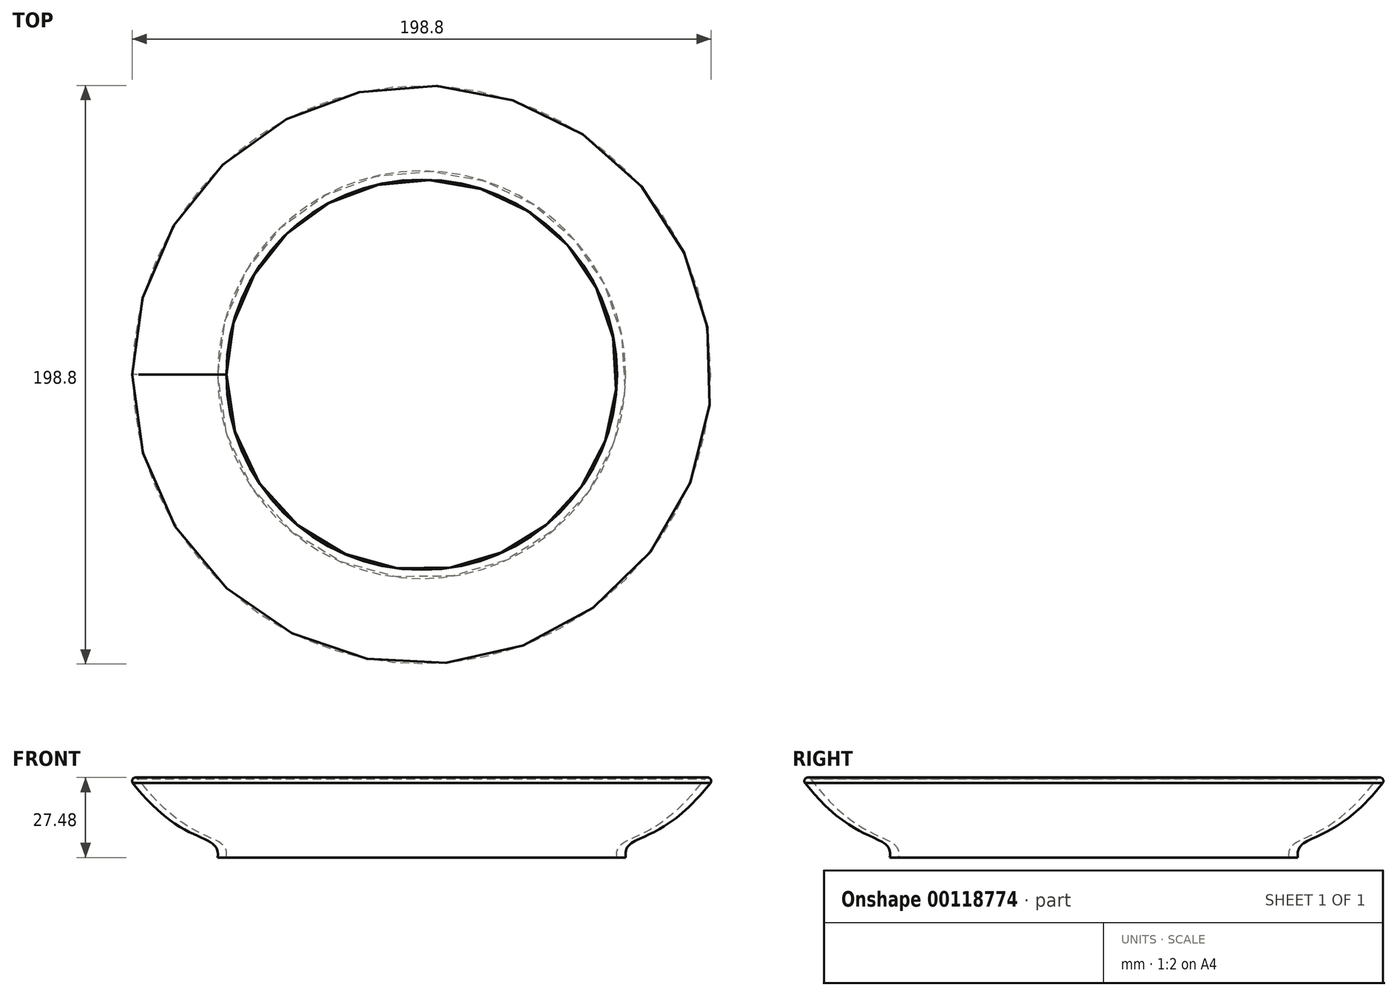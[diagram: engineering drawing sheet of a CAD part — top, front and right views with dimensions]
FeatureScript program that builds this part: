
annotation { "Feature Type Name" : "Feature", "Feature Type Description" : "" }
export const myFeature = defineFeature(function(context is Context, id is Id, definition is map)
    precondition{}
    {
        {
            var Q0;
            Q0=qCreatedBy(makeId("Top.planeOp"),FACE);
            var sketch = newSketch(context, id + "F0", { "sketchPlane" : qUnion([Q0])});
            skCircle(sketch, "E0", {"center": v(0, 0) * mm, "radius": 69.75 * mm});
            skCircle(sketch, "E1", {"center": v(0, 0) * mm, "radius": 70.05 * mm});
            skPoint(sketch, "E2", {"position": v(-69.9, 0) * mm});
            skSolve(sketch);
        }
        {
            var Q0;
            Q0=qCreatedBy(makeId("Top.planeOp"),FACE);
            cPlane(context, id + "F1", {"entities" : qUnion([Q0]), "cplaneType" : CPlaneType.OFFSET, "offset" : 27 * mm, "width" : 150 * mm, "height" : 150 * mm});
        }
        {
            var Q0;
            Q0=qCreatedBy(id+"F1.planeOp",FACE);
            var sketch = newSketch(context, id + "F2", { "sketchPlane" : qUnion([Q0])});
            skPoint(sketch, "E3", {"position": v(-100.25, 0) * mm});
            skSolve(sketch);
        }
        {
            var Q0;
            Q0=qCreatedBy(makeId("Front.planeOp"),FACE);
            var sketch = newSketch(context, id + "F3", { "sketchPlane" : qUnion([Q0])});
            skPoint(sketch, "E4", {"position": v(-70.05, 0) * mm});
            skPoint(sketch, "E5", {"position": v(-100.25, 27) * mm});
            skFitSpline(sketch, "E6", {"points": [v(-70.05, 0) * mm, v(-100.25, 27) * mm], "startDerivative": vector(3.53, 27.64) * mm, "endDerivative": vector(-54.32, 72.91) * mm});
            skFitSpline(sketch, "E7", {"points": [v(-67.05, 0) * mm, v(-97.25, 27) * mm], "startDerivative": vector(3.52, 27.58) * mm, "endDerivative": vector(-54.2, 72.76) * mm});
            skLineSegment(sketch, "E8", {"start": v(-97.25, 27) * mm, "end": v(-99.2, 25.62) * mm});
            skArc(sketch, "E9", {"start": v(-97.25, 27) * mm, "mid": v(-98.9, 27.26) * mm, "end": v(-99.2, 25.62) * mm});
            skLineSegment(sketch, "E10", {"start": v(-70.05, 0) * mm, "end": v(-67.05, 0) * mm});
            skSolve(sketch);
        }
        {
            var Q0;
            Q0=qCreatedBy(makeId("Front.planeOp"),FACE);
            var sketch = newSketch(context, id + "F4", { "sketchPlane" : qUnion([Q0])});
            skLineSegment(sketch, "E11", {"start": v(0, 0) * mm, "end": v(0, 47.29) * mm});
            skSolve(sketch);
        }
        {
            var Q0;
            Q0=makeQuery(id+"F3.imprint","IMPRINT",FACE,{"disambiguationData":[TD([[makeQuery(id+"F3.imprint","IMPRINT",EDGE,{"derivedFrom":sQuery(id+"F3.wireOp",EDGE,"E7")}),1.0]])]});
            var Q1;
            Q1=makeQuery(id+"F3.imprint","IMPRINT",FACE,{"disambiguationData":[TD([[makeQuery(id+"F3.imprint","IMPRINT",EDGE,{"derivedFrom":sQuery(id+"F3.wireOp",EDGE,"E8")}),-1.0]])]});
            var Q2;
            Q2=sQuery(id+"F4.wireOp",EDGE,"E11");
            revolve(context, id + "F5", {"entities" : qUnion([Q0, Q1]), "axis" : qUnion([Q2]), "revolveType" : RevolveType.FULL});
        }
    });
